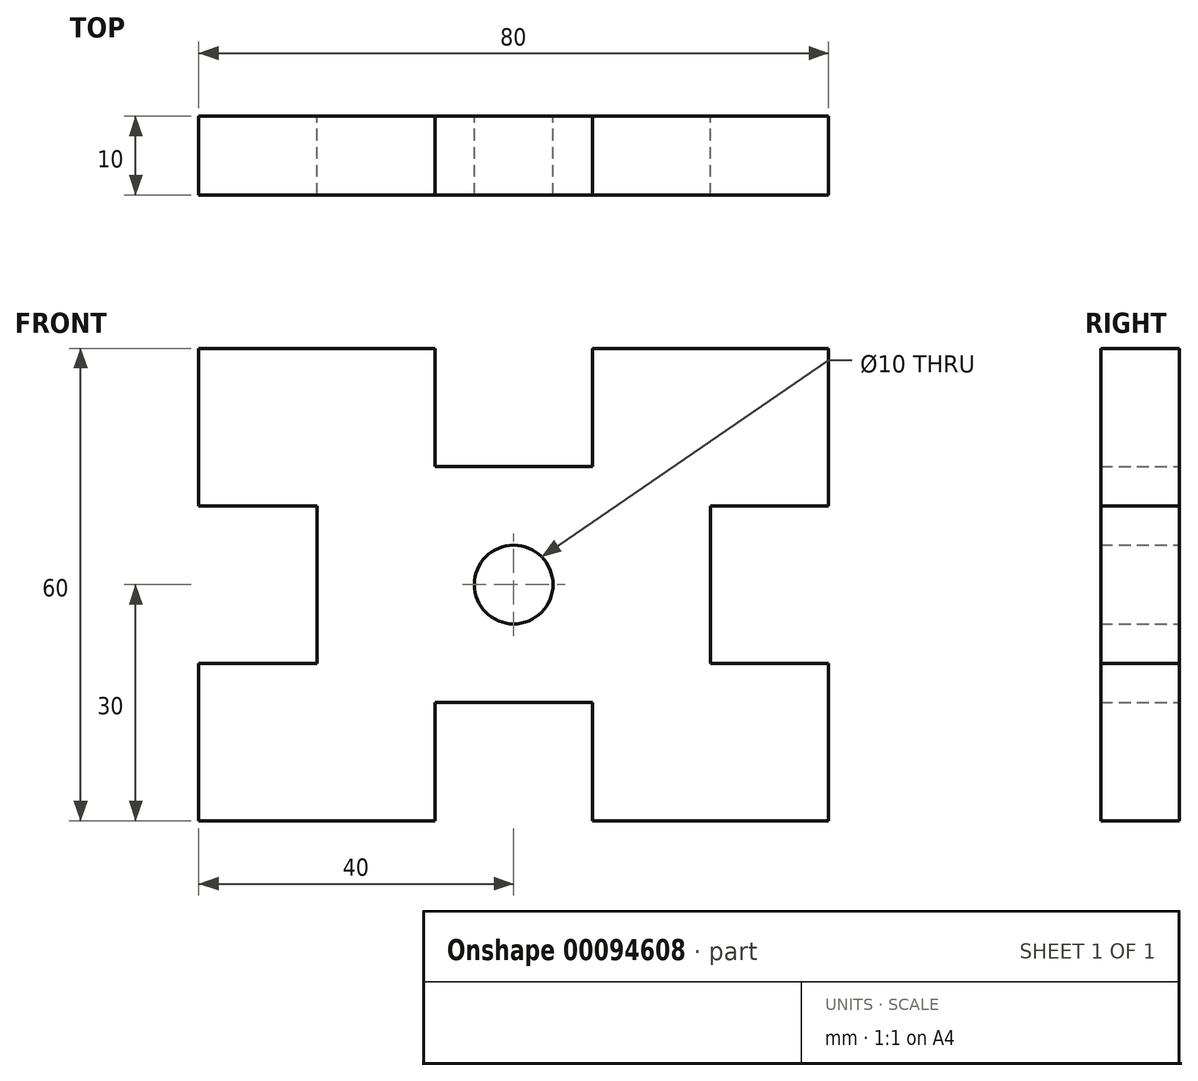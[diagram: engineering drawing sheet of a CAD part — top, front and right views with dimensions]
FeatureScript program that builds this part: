
annotation { "Feature Type Name" : "Feature", "Feature Type Description" : "" }
export const myFeature = defineFeature(function(context is Context, id is Id, definition is map)
    precondition{}
    {
        {
            var Q0;
            Q0=qCreatedBy(makeId("Front.planeOp"),FACE);
            var sketch = newSketch(context, id + "F0", { "sketchPlane" : qUnion([Q0])});
            skLineSegment(sketch, "E0", {"start": v(0, 21) * mm, "end": v(0, -23.64) * mm, "construction": true});
            skLineSegment(sketch, "E1", {"start": v(-27.6, 0) * mm, "end": v(29.15, 0) * mm, "construction": true});
            skLineSegment(sketch, "E2", {"start": v(-25, 0) * mm, "end": v(-25, 10) * mm});
            skLineSegment(sketch, "E3", {"start": v(-25, 10) * mm, "end": v(-40, 10) * mm});
            skLineSegment(sketch, "E4", {"start": v(-40, 10) * mm, "end": v(-40, 30) * mm});
            skLineSegment(sketch, "E5", {"start": v(-40, 30) * mm, "end": v(-10, 30) * mm});
            skLineSegment(sketch, "E6", {"start": v(-10, 30) * mm, "end": v(-10, 15) * mm});
            skLineSegment(sketch, "E7", {"start": v(-10, 15) * mm, "end": v(0, 15) * mm});
            skLineSegment(sketch, "E8.MirrorCS", {"start": v(10, 30) * mm, "end": v(10, 15) * mm});
            skLineSegment(sketch, "E9.MirrorCS", {"start": v(40, 10) * mm, "end": v(40, 30) * mm});
            skLineSegment(sketch, "E10.MirrorCS", {"start": v(25, 10) * mm, "end": v(40, 10) * mm});
            skLineSegment(sketch, "E11.MirrorCS", {"start": v(40, 30) * mm, "end": v(10, 30) * mm});
            skLineSegment(sketch, "E12.MirrorCS", {"start": v(10, 15) * mm, "end": v(0, 15) * mm});
            skLineSegment(sketch, "E13.MirrorCS", {"start": v(25, 0) * mm, "end": v(25, 10) * mm});
            skLineSegment(sketch, "E14.MirrorCS", {"start": v(10, -30) * mm, "end": v(10, -15) * mm});
            skLineSegment(sketch, "E15.MirrorCS", {"start": v(-10, -30) * mm, "end": v(-10, -15) * mm});
            skLineSegment(sketch, "E16.MirrorCS", {"start": v(-10, -15) * mm, "end": v(0, -15) * mm});
            skLineSegment(sketch, "E17.MirrorCS", {"start": v(25, -10) * mm, "end": v(40, -10) * mm});
            skLineSegment(sketch, "E18.MirrorCS", {"start": v(-40, -10) * mm, "end": v(-40, -30) * mm});
            skLineSegment(sketch, "E19.MirrorCS", {"start": v(-40, -30) * mm, "end": v(-10, -30) * mm});
            skLineSegment(sketch, "E20.MirrorCS", {"start": v(25, 0) * mm, "end": v(25, -10) * mm});
            skLineSegment(sketch, "E21.MirrorCS", {"start": v(40, -10) * mm, "end": v(40, -30) * mm});
            skLineSegment(sketch, "E22.MirrorCS", {"start": v(-25, -10) * mm, "end": v(-40, -10) * mm});
            skLineSegment(sketch, "E23.MirrorCS", {"start": v(40, -30) * mm, "end": v(10, -30) * mm});
            skLineSegment(sketch, "E24.MirrorCS", {"start": v(-25, 0) * mm, "end": v(-25, -10) * mm});
            skLineSegment(sketch, "E25.MirrorCS", {"start": v(10, -15) * mm, "end": v(0, -15) * mm});
            skCircle(sketch, "E26", {"center": v(0, 0) * mm, "radius": 5 * mm});
            skSolve(sketch);
        }
        {
            var Q0;
            Q0 = qSketchRegion(id + "F0", true);
            extrude(context, id + "F1", {"entities" : qUnion([Q0]), "depth" : 10 * mm});
        }
    });
